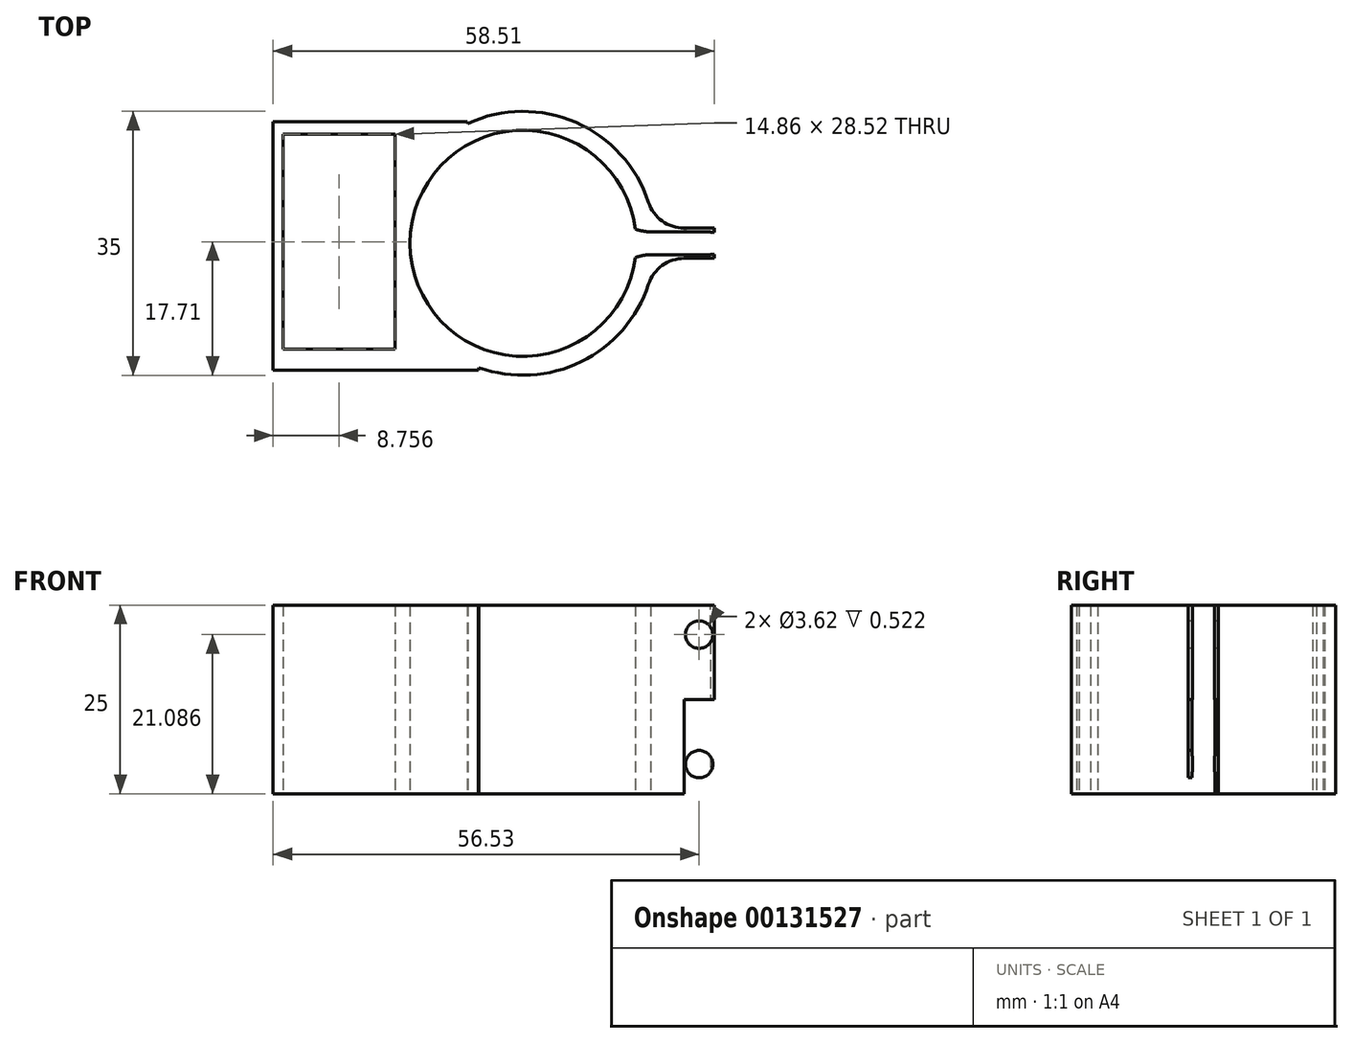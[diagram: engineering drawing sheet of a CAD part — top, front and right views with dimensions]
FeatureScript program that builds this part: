
annotation { "Feature Type Name" : "Feature", "Feature Type Description" : "" }
export const myFeature = defineFeature(function(context is Context, id is Id, definition is map)
    precondition{}
    {
        {
            var Q0;
            Q0=qCreatedBy(makeId("Front.planeOp"),FACE);
            var sketch = newSketch(context, id + "F0", { "sketchPlane" : qUnion([Q0])});
            skLineSegment(sketch, "E0", {"start": v(0, 0) * mm, "end": v(0, 32.52) * mm});
            skLineSegment(sketch, "E1", {"start": v(0, 32.52) * mm, "end": v(43.59, 32.52) * mm});
            skLineSegment(sketch, "E2", {"start": v(43.59, 32.52) * mm, "end": v(43.59, 26.32) * mm});
            skLineSegment(sketch, "E3", {"start": v(43.59, 26.32) * mm, "end": v(8, 26.32) * mm});
            skLineSegment(sketch, "E4", {"start": v(8, 26.32) * mm, "end": v(8, 0) * mm});
            skLineSegment(sketch, "E5", {"start": v(8, 0) * mm, "end": v(8, -20.35) * mm});
            skLineSegment(sketch, "E6", {"start": v(8, -20.35) * mm, "end": v(43.59, -20.35) * mm});
            skLineSegment(sketch, "E7", {"start": v(43.59, -20.35) * mm, "end": v(43.59, -28.33) * mm});
            skLineSegment(sketch, "E8", {"start": v(43.59, -28.33) * mm, "end": v(0, -28.33) * mm});
            skLineSegment(sketch, "E9", {"start": v(0, -28.33) * mm, "end": v(0, 0) * mm});
            skSolve(sketch);
        }
        {
            var Q0;
            Q0 = qSketchRegion(id + "F0", true);
            extrude(context, id + "F1", {"entities" : qUnion([Q0]), "depth" : 80 * mm});
        }
        {
            var Q0;
            Q0=makeQuery(id+"F1.opExtrude","SWEPT_FACE",FACE,{"disambiguationData":[OSD([sQuery(id+"F0.wireOp",EDGE,"E1")])]});
            var sketch = newSketch(context, id + "F2", { "sketchPlane" : qUnion([Q0])});
            skCircle(sketch, "E10", {"center": v(32.25, -37.83) * mm, "radius": 9.49 * mm});
            skSolve(sketch);
        }
        {
            var Q0;
            Q0=makeQuery(id+"F2.imprint","IMPRINT",FACE,{"disambiguationData":[TD([[makeQuery(id+"F2.imprint","IMPRINT",EDGE,{"derivedFrom":sQuery(id+"F2.wireOp",EDGE,"E10")}),1.0]])]});
            extrude(context, id + "F3", {"entities" : qUnion([Q0]), "operationType" : NewBodyOperationType.ADD, "depth" : 600 * mm});
        }
        {
            var Q0;
            Q0=makeQuery(id+"F3.opExtrude","CAP_FACE",FACE,{"disambiguationData":[OSD([sQuery(id+"F2.wireOp",EDGE,"E10")])],"isStart":false});
            var sketch = newSketch(context, id + "F4", { "sketchPlane" : qUnion([Q0])});
            skLineSegment(sketch, "E11.bottom", {"start": v(20.9, -38.62) * mm, "end": v(24.96, -38.62) * mm});
            skLineSegment(sketch, "E11.top", {"start": v(20.9, -36.4) * mm, "end": v(24.96, -36.4) * mm});
            skLineSegment(sketch, "E11.left", {"start": v(20.9, -38.62) * mm, "end": v(20.9, -36.4) * mm});
            skLineSegment(sketch, "E11.right", {"start": v(24.96, -38.62) * mm, "end": v(24.96, -36.4) * mm});
            skSolve(sketch);
        }
        {
            var Q0;
            Q0 = qSketchRegion(id + "F4", true);
            extrude(context, id + "F5", {"entities" : qUnion([Q0]), "operationType" : NewBodyOperationType.REMOVE, "oppositeDirection" : true, "depth" : 15 * mm});
        }
        {
            var Q0;
            Q0=makeQuery(id+"F3.opExtrude","CAP_FACE",FACE,{"disambiguationData":[OSD([sQuery(id+"F2.wireOp",EDGE,"E10")])],"isStart":false});
            var sketch = newSketch(context, id + "F6", { "sketchPlane" : qUnion([Q0])});
            skCircle(sketch, "E12", {"center": v(32.25, -37.83) * mm, "radius": 8 * mm});
            skSolve(sketch);
        }
        {
            var Q0;
            Q0 = qSketchRegion(id + "F6", true);
            extrude(context, id + "F7", {"entities" : qUnion([Q0]), "operationType" : NewBodyOperationType.REMOVE, "oppositeDirection" : true, "depth" : 600 * mm});
        }
        {
            var Q0;
            Q0=makeQuery(id+"F7.boolean.opBoolean","COPY",FACE,{"derivedFrom":makeQuery(id+"F7.opExtrude","CAP_FACE",FACE,{"disambiguationData":[OSD([sQuery(id+"F6.wireOp",EDGE,"E12")])],"isStart":false})});
            var sketch = newSketch(context, id + "F8", { "sketchPlane" : qUnion([Q0])});
            skCircle(sketch, "E13", {"center": v(32.25, -37.83) * mm, "radius": 7.62 * mm});
            skSolve(sketch);
        }
        {
            var Q0;
            Q0 = qSketchRegion(id + "F8", true);
            extrude(context, id + "F9", {"entities" : qUnion([Q0]), "depth" : 620 * mm, "hasSecondDirection" : true, "secondDirectionOppositeDirection" : false, "secondDirectionDepth" : 50 * mm});
        }
        {
            var Q0;
            Q0=makeQuery(id+"F9.opExtrude","CAP_FACE",FACE,{"disambiguationData":[OSD([sQuery(id+"F8.wireOp",EDGE,"E13")])],"isStart":false});
            var sketch = newSketch(context, id + "F10", { "sketchPlane" : qUnion([Q0])});
            skLineSegment(sketch, "E14.bottom", {"start": v(30.95, -31.9) * mm, "end": v(31.44, -31.9) * mm});
            skLineSegment(sketch, "E14.top", {"start": v(30.95, -23.51) * mm, "end": v(31.44, -23.51) * mm});
            skLineSegment(sketch, "E14.left", {"start": v(30.95, -31.9) * mm, "end": v(30.95, -23.51) * mm});
            skLineSegment(sketch, "E14.right", {"start": v(31.44, -31.9) * mm, "end": v(31.44, -23.51) * mm});
            skSolve(sketch);
        }
        {
            var Q0;
            Q0 = qSketchRegion(id + "F10", true);
            extrude(context, id + "F11", {"entities" : qUnion([Q0]), "operationType" : NewBodyOperationType.ADD, "oppositeDirection" : true, "depth" : 15 * mm});
        }
        {
            var Q0;
            Q0=makeQuery(id+"F11.boolean.opBoolean","MERGE",FACE,{"derivedFrom":[makeQuery(id+"F9.opExtrude","CAP_FACE",FACE,{"disambiguationData":[OSD([sQuery(id+"F8.wireOp",EDGE,"E13")])],"isStart":false}),makeQuery(id+"F11.opExtrude","CAP_FACE",FACE,{"disambiguationData":[OSD([sQuery(id+"F10.wireOp",EDGE,"E14.bottom"),sQuery(id+"F10.wireOp",EDGE,"E14.top"),sQuery(id+"F10.wireOp",EDGE,"E14.left"),sQuery(id+"F10.wireOp",EDGE,"E14.right")])],"isStart":true})]});
            var sketch = newSketch(context, id + "F12", { "sketchPlane" : qUnion([Q0])});
            skCircle(sketch, "E15", {"center": v(32.25, -37.83) * mm, "radius": 7.62 * mm});
            skLineSegment(sketch, "E16", {"start": v(24.85, -35.98) * mm, "end": v(39.65, -35.98) * mm});
            skLineSegment(sketch, "E17", {"start": v(39.65, -35.98) * mm, "end": v(39.65, 264.02) * mm});
            skLineSegment(sketch, "E18", {"start": v(24.85, -35.98) * mm, "end": v(24.85, 264.02) * mm});
            skLineSegment(sketch, "E19", {"start": v(24.85, 264.02) * mm, "end": v(39.65, 264.02) * mm});
            skSolve(sketch);
        }
        {
            var Q0;
            Q0 = qSketchRegion(id + "F12", true);
            extrude(context, id + "F13", {"entities" : qUnion([Q0]), "operationType" : NewBodyOperationType.ADD, "depth" : 25 * mm});
        }
        {
            var Q0;
            Q0=makeQuery(id+"F13.opExtrude","CAP_FACE",FACE,{"disambiguationData":[OSD([sQuery(id+"F12.wireOp",EDGE,"E15"),sQuery(id+"F12.wireOp",EDGE,"E17"),sQuery(id+"F12.wireOp",EDGE,"E18"),sQuery(id+"F12.wireOp",EDGE,"E19")])],"isStart":false});
            var sketch = newSketch(context, id + "F14", { "sketchPlane" : qUnion([Q0])});
            skLineSegment(sketch, "E20", {"start": v(24.85, 264.02) * mm, "end": v(154.85, 264.02) * mm});
            skLineSegment(sketch, "E21", {"start": v(154.85, 264.02) * mm, "end": v(154.85, -20.98) * mm});
            skLineSegment(sketch, "E22", {"start": v(154.85, -20.98) * mm, "end": v(-72.64, -20.98) * mm});
            skLineSegment(sketch, "E23", {"start": v(-72.64, -20.98) * mm, "end": v(-72.64, 264.02) * mm});
            skLineSegment(sketch, "E24", {"start": v(-72.64, 264.02) * mm, "end": v(24.85, 264.02) * mm});
            skSolve(sketch);
        }
        {
            var Q0;
            Q0 = qSketchRegion(id + "F14", true);
            extrude(context, id + "F15", {"entities" : qUnion([Q0]), "operationType" : NewBodyOperationType.ADD, "depth" : 50 * mm});
        }
        {
            var Q0;
            Q0=makeQuery(id+"F15.opExtrude","SWEPT_FACE",FACE,{"disambiguationData":[OSD([sQuery(id+"F14.wireOp",EDGE,"E22")])]});
            var sketch = newSketch(context, id + "F16", { "sketchPlane" : qUnion([Q0])});
            skLineSegment(sketch, "E25", {"start": v(154.85, 727.52) * mm, "end": v(-52.74, 686.28) * mm});
            skLineSegment(sketch, "E26", {"start": v(-52.74, 686.28) * mm, "end": v(-72.64, 692.2) * mm});
            skLineSegment(sketch, "E27", {"start": v(-72.64, 692.2) * mm, "end": v(-81.2, 736.6) * mm});
            skLineSegment(sketch, "E28", {"start": v(-81.2, 736.6) * mm, "end": v(154.85, 727.52) * mm});
            skSolve(sketch);
        }
        {
            var Q0;
            Q0 = qSketchRegion(id + "F16", true);
            extrude(context, id + "F17", {"entities" : qUnion([Q0]), "operationType" : NewBodyOperationType.REMOVE, "oppositeDirection" : true, "depth" : 295 * mm});
        }
        {
            var Q0;
            Q0=makeQuery(id+"F1.opExtrude","SWEPT_FACE",FACE,{"disambiguationData":[OSD([sQuery(id+"F0.wireOp",EDGE,"E2")])]});
            var sketch = newSketch(context, id + "F18", { "sketchPlane" : qUnion([Q0])});
            skLineSegment(sketch, "E29.bottom", {"start": v(-80, 32.52) * mm, "end": v(0, 32.52) * mm});
            skLineSegment(sketch, "E29.top", {"start": v(-80, -28.51) * mm, "end": v(0, -28.51) * mm});
            skLineSegment(sketch, "E29.left", {"start": v(-80, 32.52) * mm, "end": v(-80, -28.51) * mm});
            skLineSegment(sketch, "E29.right", {"start": v(0, 32.52) * mm, "end": v(0, -28.51) * mm});
            skSolve(sketch);
        }
        {
            var Q0;
            Q0 = qSketchRegion(id + "F18", true);
            extrude(context, id + "F19", {"entities" : qUnion([Q0]), "depth" : 10 * mm});
        }
        {
            var Q0;
            Q0=makeQuery(id+"F15.boolean.opBoolean","MERGE",FACE,{"derivedFrom":[makeQuery(id+"F13.opExtrude","SWEPT_FACE",FACE,{"disambiguationData":[OSD([sQuery(id+"F12.wireOp",EDGE,"E19")])]}),makeQuery(id+"F15.opExtrude","SWEPT_FACE",FACE,{"disambiguationData":[OSD([sQuery(id+"F14.wireOp",EDGE,"E20"),sQuery(id+"F14.wireOp",EDGE,"E24")])]})]});
            var sketch = newSketch(context, id + "F20", { "sketchPlane" : qUnion([Q0])});
            skLineSegment(sketch, "E30.bottom", {"start": v(-114.9, 700.19) * mm, "end": v(-72.59, 700.19) * mm});
            skLineSegment(sketch, "E30.top", {"start": v(-114.9, 693.12) * mm, "end": v(-72.59, 693.12) * mm});
            skLineSegment(sketch, "E30.left", {"start": v(-114.9, 700.19) * mm, "end": v(-114.9, 693.12) * mm});
            skLineSegment(sketch, "E30.right", {"start": v(-72.59, 700.19) * mm, "end": v(-72.59, 693.12) * mm});
            skSolve(sketch);
        }
        {
            var Q0;
            Q0 = qSketchRegion(id + "F20", true);
            extrude(context, id + "F21", {"entities" : qUnion([Q0]), "operationType" : NewBodyOperationType.ADD, "depth" : 25 * mm});
        }
        {
            var Q0;
            Q0=makeQuery(id+"F21.opExtrude","SWEPT_FACE",FACE,{"disambiguationData":[OSD([sQuery(id+"F20.wireOp",EDGE,"E30.bottom")])]});
            var sketch = newSketch(context, id + "F22", { "sketchPlane" : qUnion([Q0])});
            skLineSegment(sketch, "E31.bottom", {"start": v(77.38, 268.29) * mm, "end": v(111.06, 268.29) * mm});
            skLineSegment(sketch, "E31.top", {"start": v(77.38, 284.45) * mm, "end": v(111.06, 284.45) * mm});
            skLineSegment(sketch, "E31.left", {"start": v(77.38, 268.29) * mm, "end": v(77.38, 284.45) * mm});
            skLineSegment(sketch, "E31.right", {"start": v(111.06, 268.29) * mm, "end": v(111.06, 284.45) * mm});
            skSolve(sketch);
        }
        {
            var Q0;
            Q0=makeQuery(id+"F22.imprint","IMPRINT",FACE,{"disambiguationData":[TD([[makeQuery(id+"F22.imprint","IMPRINT",EDGE,{"derivedFrom":sQuery(id+"F22.wireOp",EDGE,"E31.bottom")}),1.0]])]});
            extrude(context, id + "F23", {"entities" : qUnion([Q0]), "operationType" : NewBodyOperationType.REMOVE, "oppositeDirection" : true, "depth" : 25 * mm});
        }
        {
            var Q0;
            Q0=makeQuery(id+"F19.opExtrude","SWEPT_BODY",BODY,{"disambiguationData":[OSD([sQuery(id+"F18.wireOp",EDGE,"E29.bottom"),sQuery(id+"F18.wireOp",EDGE,"E29.top"),sQuery(id+"F18.wireOp",EDGE,"E29.left"),sQuery(id+"F18.wireOp",EDGE,"E29.right")])]});
            var Q1;
            Q1=makeQuery(id+"F9.opExtrude","SWEPT_BODY",BODY,{"disambiguationData":[OSD([sQuery(id+"F8.wireOp",EDGE,"E13")])]});
            deleteBodies(context, id + "F24", {"entities" : qUnion([Q0, Q1])});
        }
        {
            var Q0;
            Q0=makeQuery(id+"F1.opExtrude","SWEPT_BODY",BODY,{"disambiguationData":[OSD([sQuery(id+"F0.wireOp",EDGE,"E0"),sQuery(id+"F0.wireOp",EDGE,"E1"),sQuery(id+"F0.wireOp",EDGE,"E2"),sQuery(id+"F0.wireOp",EDGE,"E3"),sQuery(id+"F0.wireOp",EDGE,"E4"),sQuery(id+"F0.wireOp",EDGE,"E5"),sQuery(id+"F0.wireOp",EDGE,"E6"),sQuery(id+"F0.wireOp",EDGE,"E7"),sQuery(id+"F0.wireOp",EDGE,"E8"),sQuery(id+"F0.wireOp",EDGE,"E9")])]});
            deleteBodies(context, id + "F25", {"entities" : qUnion([Q0])});
        }
        {
            var Q0;
            Q0=qCreatedBy(makeId("Top.planeOp"),FACE);
            var sketch = newSketch(context, id + "F26", { "sketchPlane" : qUnion([Q0])});
            skArc(sketch, "E32", {"start": v(14.88, 1.88) * mm, "mid": v(-15, 0) * mm, "end": v(14.88, -1.88) * mm});
            skArc(sketch, "E33", {"start": v(17.39, 2) * mm, "mid": v(-17.5, 0) * mm, "end": v(17.39, -2) * mm});
            skLineSegment(sketch, "E34.0", {"start": v(16.9, -1.5) * mm, "end": v(24.84, -1.5) * mm});
            skLineSegment(sketch, "E35.0", {"start": v(16.9, 1.5) * mm, "end": v(24.84, 1.5) * mm});
            skLineSegment(sketch, "E36", {"start": v(24.84, 1.5) * mm, "end": v(24.84, -1.5) * mm});
            skPoint(sketch, "E37.orphan", {"position": v(11.86, 0) * mm});
            skLineSegment(sketch, "E38.0", {"start": v(17.39, -2) * mm, "end": v(24.84, -2) * mm});
            skLineSegment(sketch, "E39.0", {"start": v(17.39, 2) * mm, "end": v(24.84, 2) * mm});
            skLineSegment(sketch, "E40", {"start": v(24.84, -2) * mm, "end": v(24.84, -2) * mm});
            skLineSegment(sketch, "E41", {"start": v(24.84, -2) * mm, "end": v(25.34, -2) * mm});
            skLineSegment(sketch, "E42", {"start": v(25.34, -2) * mm, "end": v(25.34, -1.5) * mm});
            skLineSegment(sketch, "E43", {"start": v(24.84, 2) * mm, "end": v(24.84, 2) * mm});
            skLineSegment(sketch, "E44", {"start": v(24.84, 2) * mm, "end": v(25.34, 2) * mm});
            skLineSegment(sketch, "E45", {"start": v(25.34, 2) * mm, "end": v(25.34, 1.5) * mm});
            skArc(sketch, "E46", {"start": v(14.88, 1.88) * mm, "mid": v(16.14, 1.57) * mm, "end": v(17.44, 1.5) * mm});
            skLineSegment(sketch, "E47", {"start": v(13.68, 0) * mm, "end": v(19.4, 0) * mm});
            skArc(sketch, "E48.MirrorCS", {"start": v(14.88, -1.88) * mm, "mid": v(16.14, -1.57) * mm, "end": v(17.44, -1.5) * mm});
            skPoint(sketch, "E49.orphan", {"position": v(14.73, -1.93) * mm});
            skPoint(sketch, "E50.orphan", {"position": v(14.73, 1.93) * mm});
            skArc(sketch, "E51.trimOffspring", {"start": v(17.44, -1.5) * mm, "mid": v(17.5, 0) * mm, "end": v(17.44, 1.5) * mm});
            skLineSegment(sketch, "E52", {"start": v(25.34, 1.5) * mm, "end": v(25.34, -1.5) * mm});
            skSolve(sketch);
        }
        {
            var Q0;
            {var subQ6=sQuery(id+"F26.wireOp",EDGE,"E32");Q0=makeQuery(id+"F26.imprint","IMPRINT",FACE,{"disambiguationData":[TD([[makeQuery(id+"F26.imprint","IMPRINT",EDGE,{"derivedFrom":subQ6}),-1.0]])]});}
            extrude(context, id + "F27", {"entities" : qUnion([Q0]), "depth" : 25 * mm});
        }
        {
            var Q0;
            Q0=makeQuery(id+"F27.opExtrude","SWEPT_EDGE",EDGE,{"disambiguationData":[OSD([sQuery(id+"F26.wireOp",EDGE,"E33"),sQuery(id+"F26.wireOp",EDGE,"E38.0")])]});
            var Q1;
            Q1=makeQuery(id+"F27.opExtrude","SWEPT_EDGE",EDGE,{"disambiguationData":[OSD([sQuery(id+"F26.wireOp",EDGE,"E33"),sQuery(id+"F26.wireOp",EDGE,"E39.0")])]});
            fillet(context, id + "F28", {"entities" : qUnion([Q0, Q1]), "radius" : 5 * mm, "tangentPropagation" : true, "allowEdgeOverflow" : false});
        }
        {
            var Q0;
            Q0=qCreatedBy(makeId("Top.planeOp"),FACE);
            var sketch = newSketch(context, id + "F29", { "sketchPlane" : qUnion([Q0])});
            skLineSegment(sketch, "E53.bottom", {"start": v(29.55, 1.48) * mm, "end": v(20.3, 1.48) * mm});
            skLineSegment(sketch, "E53.top", {"start": v(29.55, -1.48) * mm, "end": v(20.3, -1.48) * mm});
            skLineSegment(sketch, "E53.left", {"start": v(29.55, 1.48) * mm, "end": v(29.55, -1.48) * mm});
            skLineSegment(sketch, "E53.right", {"start": v(20.3, 1.48) * mm, "end": v(20.3, -1.48) * mm});
            skPoint(sketch, "E53.middle", {"position": v(24.92, 0) * mm});
            skSolve(sketch);
        }
        {
            var Q0;
            Q0 = qSketchRegion(id + "F29", true);
            extrude(context, id + "F30", {"entities" : qUnion([Q0]), "operationType" : NewBodyOperationType.REMOVE, "oppositeDirection" : true, "depth" : 25 * mm, "hasSecondDirection" : true, "secondDirectionOppositeDirection" : false, "secondDirectionDepth" : 25 * mm});
        }
        {
            var Q0;
            Q0=makeQuery(id+"F27.opExtrude","SWEPT_FACE",FACE,{"disambiguationData":[OSD([sQuery(id+"F26.wireOp",EDGE,"E38.0"),sQuery(id+"F26.wireOp",EDGE,"E41")])]});
            var sketch = newSketch(context, id + "F31", { "sketchPlane" : qUnion([Q0])});
            skCircle(sketch, "E54", {"center": v(23.36, 21.09) * mm, "radius": 1.81 * mm});
            skPoint(sketch, "E54.centerSnap0", {"position": v(23.36, 25) * mm});
            skLineSegment(sketch, "E55", {"start": v(21.38, 12.5) * mm, "end": v(29.19, 12.5) * mm});
            skCircle(sketch, "E56.MirrorC", {"center": v(23.36, 3.91) * mm, "radius": 1.81 * mm});
            skSolve(sketch);
        }
        {
            var Q0;
            Q0=makeQuery(id+"F31.imprint","IMPRINT",FACE,{"disambiguationData":[TD([[makeQuery(id+"F31.imprint","IMPRINT",EDGE,{"derivedFrom":sQuery(id+"F31.wireOp",EDGE,"E54")}),1.0]])]});
            var Q1;
            Q1=makeQuery(id+"F31.imprint","IMPRINT",FACE,{"disambiguationData":[TD([[makeQuery(id+"F31.imprint","IMPRINT",EDGE,{"derivedFrom":sQuery(id+"F31.wireOp",EDGE,"E56.MirrorC")}),-1.0]])]});
            extrude(context, id + "F32", {"entities" : qUnion([Q0, Q1]), "operationType" : NewBodyOperationType.REMOVE, "oppositeDirection" : true, "depth" : 25 * mm});
        }
        {
            var Q0;
            Q0=qCreatedBy(makeId("Top.planeOp"),FACE);
            var sketch = newSketch(context, id + "F33", { "sketchPlane" : qUnion([Q0])});
            skLineSegment(sketch, "E57", {"start": v(-5.96, -16.8) * mm, "end": v(-33.17, -16.8) * mm});
            skLineSegment(sketch, "E58", {"start": v(-33.17, -16.8) * mm, "end": v(-33.17, 16.1) * mm});
            skLineSegment(sketch, "E59", {"start": v(-33.17, 16.1) * mm, "end": v(-7.4, 16.1) * mm});
            skArc(sketch, "E60", {"start": v(-7.24, -16.3) * mm, "mid": v(-6.6, -16.57) * mm, "end": v(-5.96, -16.8) * mm});
            skLineSegment(sketch, "E61.0", {"start": v(-32.67, -16.3) * mm, "end": v(-32.67, 15.6) * mm});
            skLineSegment(sketch, "E62.0", {"start": v(-33.18, 15.6) * mm, "end": v(-33.17, 15.6) * mm});
            skArc(sketch, "E63.0", {"start": v(-7, 15.18) * mm, "mid": v(-16.84, -0.8) * mm, "end": v(-5.63, -15.86) * mm});
            skLineSegment(sketch, "E64", {"start": v(-7.4, 16.1) * mm, "end": v(-7, 15.18) * mm});
            skLineSegment(sketch, "E65", {"start": v(-5.96, -16.8) * mm, "end": v(-5.63, -15.86) * mm});
            skLineSegment(sketch, "E66.0", {"start": v(-7.24, -16.3) * mm, "end": v(-32.67, -16.3) * mm});
            skLineSegment(sketch, "E67.trimOffspring", {"start": v(-32.67, 15.6) * mm, "end": v(-7.4, 15.6) * mm});
            skLineSegment(sketch, "E68", {"start": v(-7.4, 15.6) * mm, "end": v(-7.4, 15) * mm});
            skSolve(sketch);
        }
        {
            var Q0;
            Q0 = qSketchRegion(id + "F33", true);
            extrude(context, id + "F34", {"entities" : qUnion([Q0]), "operationType" : NewBodyOperationType.ADD, "depth" : 25 * mm});
        }
        {
            var Q0;
            Q0=qCreatedBy(makeId("Top.planeOp"),FACE);
            var sketch = newSketch(context, id + "F35", { "sketchPlane" : qUnion([Q0])});
            skLineSegment(sketch, "E69.bottom", {"start": v(-31.84, 14.47) * mm, "end": v(-16.99, 14.47) * mm});
            skLineSegment(sketch, "E69.top", {"start": v(-31.84, -14.05) * mm, "end": v(-16.99, -14.05) * mm});
            skLineSegment(sketch, "E69.left", {"start": v(-31.84, 14.47) * mm, "end": v(-31.84, -14.05) * mm});
            skLineSegment(sketch, "E69.right", {"start": v(-16.99, 14.47) * mm, "end": v(-16.99, -14.05) * mm});
            skSolve(sketch);
        }
        {
            var Q0;
            Q0 = qSketchRegion(id + "F35", true);
            extrude(context, id + "F36", {"entities" : qUnion([Q0]), "operationType" : NewBodyOperationType.REMOVE, "depth" : 40 * mm});
        }
    });
